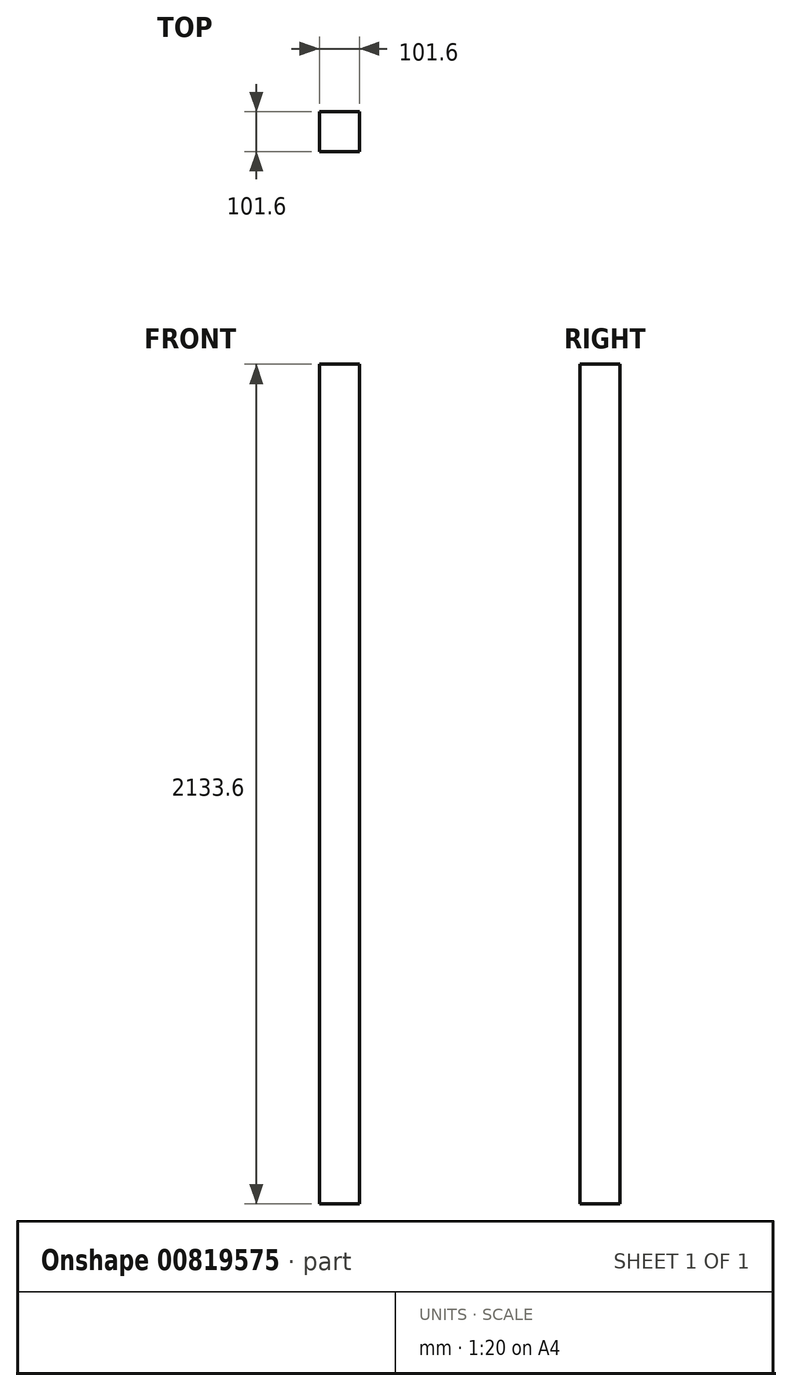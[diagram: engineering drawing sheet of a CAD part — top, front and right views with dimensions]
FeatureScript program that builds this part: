
annotation { "Feature Type Name" : "Feature", "Feature Type Description" : "" }
export const myFeature = defineFeature(function(context is Context, id is Id, definition is map)
    precondition{}
    {
        {
            var Q0;
            Q0=qCreatedBy(makeId("Top.planeOp"),FACE);
            var sketch = newSketch(context, id + "F0", { "sketchPlane" : qUnion([Q0])});
            skLineSegment(sketch, "E0.bottom", {"start": v(-50.8, 50.8) * mm, "end": v(50.8, 50.8) * mm});
            skLineSegment(sketch, "E0.top", {"start": v(-50.8, -50.8) * mm, "end": v(50.8, -50.8) * mm});
            skLineSegment(sketch, "E0.left", {"start": v(-50.8, 50.8) * mm, "end": v(-50.8, -50.8) * mm});
            skLineSegment(sketch, "E0.right", {"start": v(50.8, 50.8) * mm, "end": v(50.8, -50.8) * mm});
            skPoint(sketch, "E0.middle", {"position": v(0, 0) * mm});
            skSolve(sketch);
        }
        {
            var Q0;
            Q0 = qSketchRegion(id + "F0", true);
            extrude(context, id + "F1", {"entities" : qUnion([Q0]), "depth" : 2133.6 * mm, "offsetDistance" : 25.4 * mm});
        }
    });
